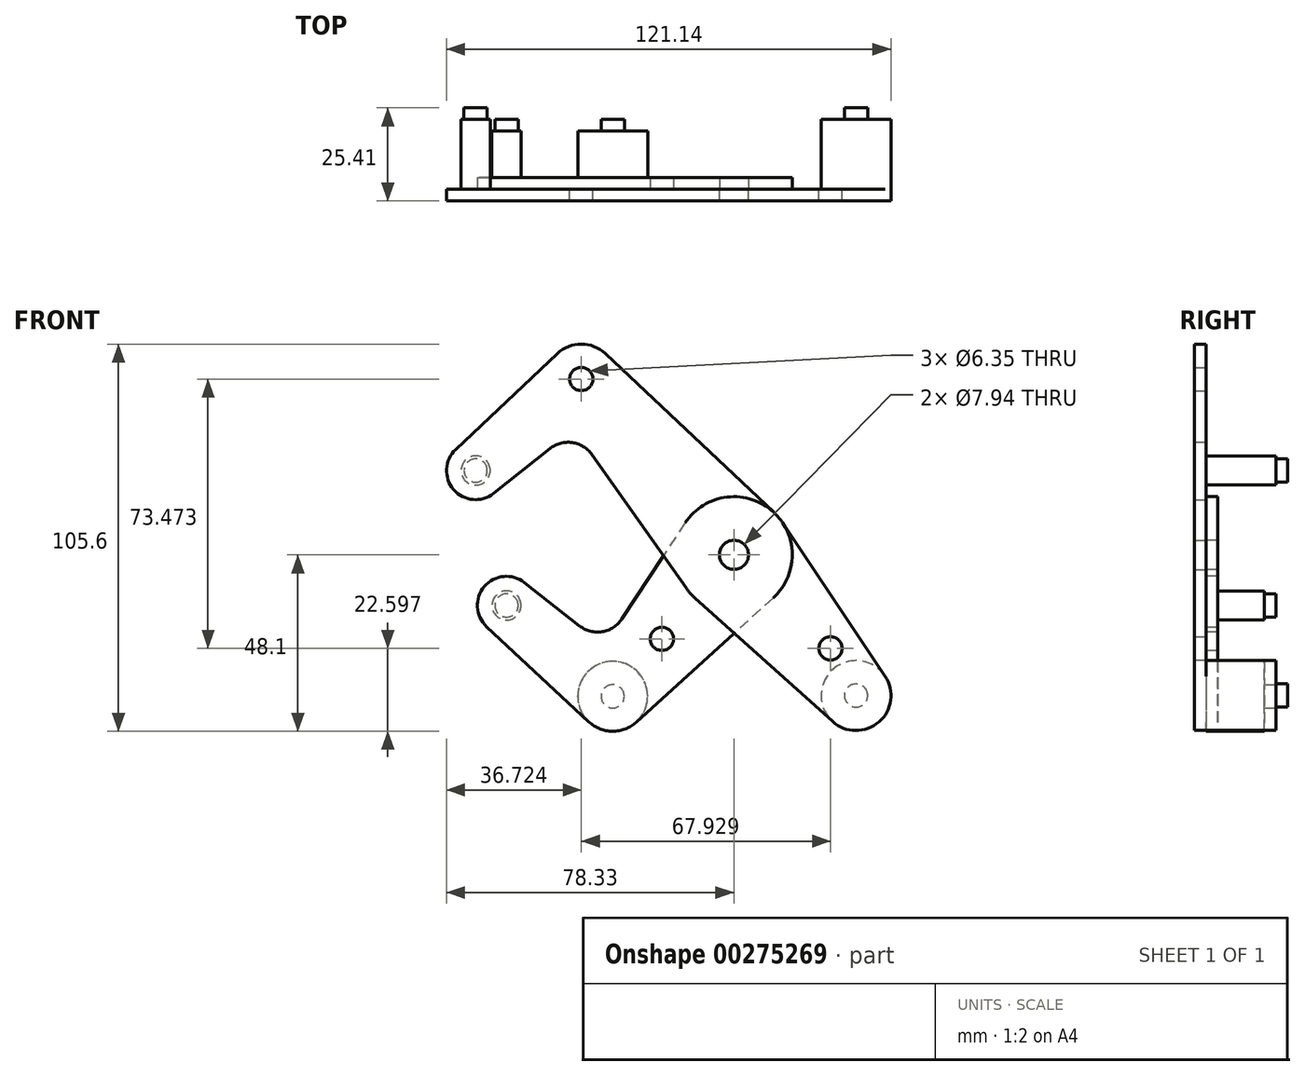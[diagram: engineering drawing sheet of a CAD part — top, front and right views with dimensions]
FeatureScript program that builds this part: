
annotation { "Feature Type Name" : "Feature", "Feature Type Description" : "" }
export const myFeature = defineFeature(function(context is Context, id is Id, definition is map)
    precondition{}
    {
        {
            var Q0;
            Q0=qCreatedBy(makeId("Front.planeOp"),FACE);
            var sketch = newSketch(context, id + "F0", { "sketchPlane" : qUnion([Q0])});
            skLineSegment(sketch, "E0", {"start": v(-41.6, 47.97) * mm, "end": v(41.6, -47.97) * mm, "construction": true});
            skCircle(sketch, "E1", {"center": v(0, 0) * mm, "radius": 3.18 * mm});
            skCircle(sketch, "E2", {"center": v(33.29, -38.38) * mm, "radius": 3.18 * mm});
            skCircle(sketch, "E3", {"center": v(-41.6, 47.97) * mm, "radius": 3.18 * mm});
            skCircle(sketch, "E4", {"center": v(-70.39, 23) * mm, "radius": 3.18 * mm});
            skLineSegment(sketch, "E5", {"start": v(-41.6, 47.97) * mm, "end": v(-70.39, 23) * mm, "construction": true});
            skCircle(sketch, "E6", {"center": v(33.29, -38.38) * mm, "radius": 9.53 * mm});
            skCircle(sketch, "E7", {"center": v(-70.39, 23) * mm, "radius": 7.94 * mm});
            skCircle(sketch, "E8", {"center": v(-41.6, 47.97) * mm, "radius": 9.53 * mm});
            skLineSegment(sketch, "E9", {"start": v(-75.83, 28.78) * mm, "end": v(-48.14, 54.9) * mm});
            skLineSegment(sketch, "E10", {"start": v(-65.44, 16.8) * mm, "end": v(-50.15, 28.98) * mm});
            skCircle(sketch, "E11", {"center": v(0, 0) * mm, "radius": 15.88 * mm});
            skLineSegment(sketch, "E12", {"start": v(-35.07, 54.9) * mm, "end": v(10.9, 11.55) * mm});
            skLineSegment(sketch, "E13", {"start": v(-38.72, 27.35) * mm, "end": v(-12.97, -9.15) * mm});
            skLineSegment(sketch, "E14", {"start": v(-10.6, -11.82) * mm, "end": v(26.93, -45.47) * mm});
            skLineSegment(sketch, "E15", {"start": v(13.2, 8.82) * mm, "end": v(41.2, -33.08) * mm});
            skArc(sketch, "E16.filletArc", {"start": v(-38.72, 27.35) * mm, "mid": v(-44.08, 30.63) * mm, "end": v(-50.15, 28.98) * mm});
            skLineSegment(sketch, "E17", {"start": v(0, 0) * mm, "end": v(-33.05, -38.58) * mm, "construction": true});
            skLineSegment(sketch, "E18", {"start": v(-33.05, -38.58) * mm, "end": v(-61.98, -13.8) * mm, "construction": true});
            skCircle(sketch, "E19", {"center": v(-61.98, -13.8) * mm, "radius": 3.18 * mm});
            skCircle(sketch, "E20", {"center": v(-33.05, -38.58) * mm, "radius": 3.18 * mm});
            skCircle(sketch, "E21", {"center": v(-61.98, -13.8) * mm, "radius": 7.94 * mm});
            skCircle(sketch, "E22", {"center": v(-33.05, -38.58) * mm, "radius": 9.53 * mm});
            skLineSegment(sketch, "E23", {"start": v(-57.08, -7.55) * mm, "end": v(-42.08, -19.35) * mm});
            skLineSegment(sketch, "E24", {"start": v(-67.4, -19.6) * mm, "end": v(-39.54, -45.55) * mm});
            skLineSegment(sketch, "E25", {"start": v(-13.25, 8.74) * mm, "end": v(-30.55, -17.48) * mm});
            skLineSegment(sketch, "E26", {"start": v(10.67, -11.75) * mm, "end": v(-26.65, -45.63) * mm});
            skArc(sketch, "E27.filletArc", {"start": v(-42.08, -19.35) * mm, "mid": v(-35.9, -20.95) * mm, "end": v(-30.55, -17.48) * mm});
            skCircle(sketch, "E28", {"center": v(-19.62, -22.9) * mm, "radius": 3.18 * mm});
            skCircle(sketch, "E29", {"center": v(26.32, -25.5) * mm, "radius": 3.18 * mm});
            skLineSegment(sketch, "E30", {"start": v(26.32, -25.5) * mm, "end": v(23.92, -27.58) * mm, "construction": true});
            skCircle(sketch, "E31", {"center": v(0, 0) * mm, "radius": 3.97 * mm});
            skSolve(sketch);
        }
        {
            var Q0;
            Q0=qCreatedBy(makeId("Front.planeOp"),FACE);
            cPlane(context, id + "F1", {"entities" : qUnion([Q0]), "cplaneType" : CPlaneType.OFFSET, "offset" : 9.52 * mm, "oppositeDirection" : true, "width" : 254 * mm, "height" : 254 * mm});
        }
        {
            var Q0;
            Q0=makeQuery(id+"F0.imprint","IMPRINT",FACE,{"disambiguationData":[TD([[makeQuery(id+"F0.imprint","IMPRINT",EDGE,{"derivedFrom":sQuery(id+"F0.wireOp",EDGE,"E2")}),-1.0]])]});
            var Q1;
            Q1=makeQuery(id+"F0.imprint","IMPRINT",FACE,{"disambiguationData":[TD([[makeQuery(id+"F0.imprint","IMPRINT",EDGE,{"derivedFrom":sQuery(id+"F0.wireOp",EDGE,"E3")}),-1.0]])]});
            var Q2;
            Q2=makeQuery(id+"F0.imprint","IMPRINT",FACE,{"disambiguationData":[TD([[makeQuery(id+"F0.imprint","IMPRINT",EDGE,{"derivedFrom":sQuery(id+"F0.wireOp",EDGE,"E4")}),-1.0]])]});
            var Q3;
            {var subQ0=sQuery(id+"F0.wireOp",EDGE,"E13");var subQ1=sQuery(id+"F0.wireOp",EDGE,"E11");var subQ2=makeQuery(id+"F0.imprint","INTERSECT",VERTEX,{"derivedFrom":[subQ1,subQ0]});Q3=makeQuery(id+"F0.imprint","IMPRINT",FACE,{"disambiguationData":[TD([[makeQuery(id+"F0.imprint","IMPRINT",EDGE,{"disambiguationData":[TD([[subQ2,1.0]])],"derivedFrom":subQ1}),-1.0]])]});}
            var Q4;
            {var subQ0=sQuery(id+"F0.wireOp",EDGE,"E14");var subQ1=sQuery(id+"F0.wireOp",EDGE,"E11");var subQ2=makeQuery(id+"F0.imprint","INTERSECT",VERTEX,{"derivedFrom":[subQ1,subQ0]});Q4=makeQuery(id+"F0.imprint","IMPRINT",FACE,{"disambiguationData":[TD([[makeQuery(id+"F0.imprint","IMPRINT",EDGE,{"disambiguationData":[TD([[subQ2,-1.0]])],"derivedFrom":subQ1}),-1.0]])]});}
            var Q5;
            {var subQ0=sQuery(id+"F0.wireOp",EDGE,"E15");Q5=makeQuery(id+"F0.imprint","IMPRINT",FACE,{"disambiguationData":[TD([[makeQuery(id+"F0.imprint","IMPRINT",EDGE,{"derivedFrom":subQ0}),-1.0]])]});}
            var Q6;
            {var subQ1=sQuery(id+"F0.wireOp",EDGE,"E9");Q6=makeQuery(id+"F0.imprint","IMPRINT",FACE,{"disambiguationData":[TD([[makeQuery(id+"F0.imprint","IMPRINT",EDGE,{"derivedFrom":subQ1}),-1.0]])]});}
            var Q7;
            Q7=makeQuery(id+"F0.imprint","IMPRINT",FACE,{"disambiguationData":[TD([[makeQuery(id+"F0.imprint","IMPRINT",EDGE,{"derivedFrom":sQuery(id+"F0.wireOp",EDGE,"E31")}),-1.0]])]});
            extrude(context, id + "F2", {"entities" : qUnion([Q0, Q1, Q2, Q3, Q4, Q5, Q6, Q7]), "depth" : 3.17 * mm});
        }
        {
            var Q0;
            Q0=makeQuery(id+"F0.imprint","IMPRINT",FACE,{"disambiguationData":[TD([[makeQuery(id+"F0.imprint","IMPRINT",EDGE,{"derivedFrom":sQuery(id+"F0.wireOp",EDGE,"E31")}),-1.0]])]});
            var Q1;
            {var subQ0=sQuery(id+"F0.wireOp",EDGE,"E14");var subQ1=sQuery(id+"F0.wireOp",EDGE,"E11");var subQ2=makeQuery(id+"F0.imprint","INTERSECT",VERTEX,{"derivedFrom":[subQ1,subQ0]});Q1=makeQuery(id+"F0.imprint","IMPRINT",FACE,{"disambiguationData":[TD([[makeQuery(id+"F0.imprint","IMPRINT",EDGE,{"disambiguationData":[TD([[subQ2,-1.0]])],"derivedFrom":subQ1}),-1.0]])]});}
            var Q2;
            {var subQ0=sQuery(id+"F0.wireOp",EDGE,"E13");var subQ1=sQuery(id+"F0.wireOp",EDGE,"E11");var subQ2=makeQuery(id+"F0.imprint","INTERSECT",VERTEX,{"derivedFrom":[subQ1,subQ0]});Q2=makeQuery(id+"F0.imprint","IMPRINT",FACE,{"disambiguationData":[TD([[makeQuery(id+"F0.imprint","IMPRINT",EDGE,{"disambiguationData":[TD([[subQ2,1.0]])],"derivedFrom":subQ1}),-1.0]])]});}
            var Q3;
            {var subQ10=sQuery(id+"F0.wireOp",EDGE,"E23");Q3=makeQuery(id+"F0.imprint","IMPRINT",FACE,{"disambiguationData":[TD([[makeQuery(id+"F0.imprint","IMPRINT",EDGE,{"derivedFrom":subQ10}),-1.0]])]});}
            var Q4;
            Q4=makeQuery(id+"F0.imprint","IMPRINT",FACE,{"disambiguationData":[TD([[makeQuery(id+"F0.imprint","IMPRINT",EDGE,{"derivedFrom":sQuery(id+"F0.wireOp",EDGE,"E20")}),-1.0]])]});
            var Q5;
            Q5=makeQuery(id+"F0.imprint","IMPRINT",FACE,{"disambiguationData":[TD([[makeQuery(id+"F0.imprint","IMPRINT",EDGE,{"derivedFrom":sQuery(id+"F0.wireOp",EDGE,"E19")}),-1.0]])]});
            extrude(context, id + "F3", {"entities" : qUnion([Q0, Q1, Q2, Q3, Q4, Q5]), "oppositeDirection" : true, "depth" : 3.17 * mm});
        }
        {
            var Q0;
            Q0=makeQuery(id+"F2.opExtrude","CAP_FACE",FACE,{"disambiguationData":[OSD([sQuery(id+"F0.wireOp",EDGE,"E2"),sQuery(id+"F0.wireOp",EDGE,"E3"),sQuery(id+"F0.wireOp",EDGE,"E4"),sQuery(id+"F0.wireOp",EDGE,"E6"),sQuery(id+"F0.wireOp",EDGE,"E7"),sQuery(id+"F0.wireOp",EDGE,"E8"),sQuery(id+"F0.wireOp",EDGE,"E9"),sQuery(id+"F0.wireOp",EDGE,"E10"),sQuery(id+"F0.wireOp",EDGE,"E11"),sQuery(id+"F0.wireOp",EDGE,"E12"),sQuery(id+"F0.wireOp",EDGE,"E13"),sQuery(id+"F0.wireOp",EDGE,"E14"),sQuery(id+"F0.wireOp",EDGE,"E15"),sQuery(id+"F0.wireOp",EDGE,"E16.filletArc"),sQuery(id+"F0.wireOp",EDGE,"E29"),sQuery(id+"F0.wireOp",EDGE,"E31")])],"isStart":false});
            var sketch = newSketch(context, id + "F4", { "sketchPlane" : qUnion([Q0])});
            skCircle(sketch, "E32", {"center": v(33.29, -38.38) * mm, "radius": 9.53 * mm});
            skCircle(sketch, "E33", {"center": v(-70.39, 23) * mm, "radius": 3.98 * mm});
            skSolve(sketch);
        }
        {
            var Q0;
            Q0=makeQuery(id+"F3.opExtrude","CAP_FACE",FACE,{"disambiguationData":[OSD([sQuery(id+"F0.wireOp",EDGE,"E11"),sQuery(id+"F0.wireOp",EDGE,"E19"),sQuery(id+"F0.wireOp",EDGE,"E20"),sQuery(id+"F0.wireOp",EDGE,"E21"),sQuery(id+"F0.wireOp",EDGE,"E22"),sQuery(id+"F0.wireOp",EDGE,"E23"),sQuery(id+"F0.wireOp",EDGE,"E24"),sQuery(id+"F0.wireOp",EDGE,"E25"),sQuery(id+"F0.wireOp",EDGE,"E26"),sQuery(id+"F0.wireOp",EDGE,"E27.filletArc"),sQuery(id+"F0.wireOp",EDGE,"E28"),sQuery(id+"F0.wireOp",EDGE,"E31")])],"isStart":true});
            var sketch = newSketch(context, id + "F5", { "sketchPlane" : qUnion([Q0])});
            skCircle(sketch, "E34", {"center": v(-33.05, -38.58) * mm, "radius": 9.53 * mm});
            skCircle(sketch, "E35", {"center": v(-61.98, -13.8) * mm, "radius": 3.98 * mm});
            skSolve(sketch);
        }
        {
            var Q0;
            Q0 = qSketchRegion(id + "F4", true);
            var Q1;
            Q1 = qSketchRegion(id + "F5", true);
            var Q2;
            Q2=qCreatedBy(id+"F1.planeOp",FACE);
            extrude(context, id + "F6", {"entities" : qUnion([Q0, Q1]), "endBound" : BoundingType.UP_TO_SURFACE, "oppositeDirection" : true, "endBoundEntityFace" : qUnion([Q2]), "depth" : 16.5 * mm});
        }
        {
            var Q0;
            Q0=makeQuery(id+"F2.opExtrude","SWEPT_BODY",BODY,{"disambiguationData":[OSD([sQuery(id+"F0.wireOp",EDGE,"E2"),sQuery(id+"F0.wireOp",EDGE,"E3"),sQuery(id+"F0.wireOp",EDGE,"E4"),sQuery(id+"F0.wireOp",EDGE,"E6"),sQuery(id+"F0.wireOp",EDGE,"E7"),sQuery(id+"F0.wireOp",EDGE,"E8"),sQuery(id+"F0.wireOp",EDGE,"E9"),sQuery(id+"F0.wireOp",EDGE,"E10"),sQuery(id+"F0.wireOp",EDGE,"E11"),sQuery(id+"F0.wireOp",EDGE,"E12"),sQuery(id+"F0.wireOp",EDGE,"E13"),sQuery(id+"F0.wireOp",EDGE,"E14"),sQuery(id+"F0.wireOp",EDGE,"E15"),sQuery(id+"F0.wireOp",EDGE,"E16.filletArc"),sQuery(id+"F0.wireOp",EDGE,"E29"),sQuery(id+"F0.wireOp",EDGE,"E31")])]});
            var Q1;
            Q1=makeQuery(id+"F3.opExtrude","SWEPT_BODY",BODY,{"disambiguationData":[OSD([sQuery(id+"F0.wireOp",EDGE,"E11"),sQuery(id+"F0.wireOp",EDGE,"E19"),sQuery(id+"F0.wireOp",EDGE,"E20"),sQuery(id+"F0.wireOp",EDGE,"E21"),sQuery(id+"F0.wireOp",EDGE,"E22"),sQuery(id+"F0.wireOp",EDGE,"E23"),sQuery(id+"F0.wireOp",EDGE,"E24"),sQuery(id+"F0.wireOp",EDGE,"E25"),sQuery(id+"F0.wireOp",EDGE,"E26"),sQuery(id+"F0.wireOp",EDGE,"E27.filletArc"),sQuery(id+"F0.wireOp",EDGE,"E28"),sQuery(id+"F0.wireOp",EDGE,"E31")])]});
            var Q2;
            Q2=makeQuery(id+"F6.opExtrude","SWEPT_BODY",BODY,{"disambiguationData":[OSD([sQuery(id+"F4.wireOp",EDGE,"E32")])]});
            var Q3;
            Q3=makeQuery(id+"F6.opExtrude","SWEPT_BODY",BODY,{"disambiguationData":[OSD([sQuery(id+"F4.wireOp",EDGE,"E33")])]});
            var Q4;
            Q4=makeQuery(id+"F6.opExtrude","SWEPT_BODY",BODY,{"disambiguationData":[OSD([sQuery(id+"F5.wireOp",EDGE,"E34")])]});
            var Q5;
            Q5=makeQuery(id+"F6.opExtrude","SWEPT_BODY",BODY,{"disambiguationData":[OSD([sQuery(id+"F5.wireOp",EDGE,"E35")])]});
            booleanBodies(context, id + "F7", {"operationType" : BooleanOperationType.SUBTRACTION, "tools" : qUnion([Q0, Q1]), "targets" : qUnion([Q2, Q3, Q4, Q5]), "keepTools" : true});
        }
        {
            var Q0;
            Q0=makeQuery(id+"F6.opExtrude","SWEPT_BODY",BODY,{"disambiguationData":[OSD([sQuery(id+"F4.wireOp",EDGE,"E32")])]});
            var Q1;
            Q1=makeQuery(id+"F6.opExtrude","SWEPT_BODY",BODY,{"disambiguationData":[OSD([sQuery(id+"F4.wireOp",EDGE,"E33")])]});
            var Q2;
            Q2=makeQuery(id+"F6.opExtrude","SWEPT_BODY",BODY,{"disambiguationData":[OSD([sQuery(id+"F5.wireOp",EDGE,"E34")])]});
            var Q3;
            Q3=makeQuery(id+"F6.opExtrude","SWEPT_BODY",BODY,{"disambiguationData":[OSD([sQuery(id+"F5.wireOp",EDGE,"E35")])]});
            var Q4;
            Q4=qCreatedBy(id+"F1.planeOp",FACE);
            mirror(context, id + "F8", {"operationType" : NewBodyOperationType.ADD, "entities" : qUnion([Q0, Q1, Q2, Q3]), "mirrorPlane" : qUnion([Q4])});
        }
    });
